# Revit family: QF_BOURGEAT_Lave_mains_cuve_ronde
name_source: partatom
category: Appareils sanitaires
revit_build: Autodesk Revit 2015 (Build: 20140606_1530(x64)
units: mm (PartAtom-declared; Revit-internal decimal feet)

## types (2) — shared parameters
Capacité de la cuve = 5 L
Certification = NF hygiene alimentaire
Diamètre de Raccordement Eau Adoucie = 21 mm
Diamètre de Raccordement Evacuation = 32 mm
Diamétre de la cuve = 275 mm
Débit Eau Adoucie = 0.2 L/s
Fabricant = BOURGEAT
Hauteur de la cuve = 125 mm  [stored 0.410105 ft]
Longueur hors tout = 340 mm  [stored 1.11549 ft]
Raccord = 15/21
Spécification du Fabricant = Lave mains à cuve ronde
URL catalogue = http://www.bourgeat.fr
zero-valued in all types: Hauteur de Raccordement Eau Adoucie du Sol Finis

## per-type parameters (varying)
| type | Dosseret | Hauteur hors tout | Modèle | Poids net à vide | Profondeur hors tout | position |
| Lave-mains sans dosseret | Non | 360 mm  [stored 1.1811 ft] | 849600 | 4.00 kg | 340 mm  [stored 1.11549 ft] | 1 mm  [stored 0.00328084 ft] |
| Lave-mains avec dosseret | Oui | 530 mm  [stored 1.73885 ft] | 849800 | 5.00 kg | 365 mm  [stored 1.19751 ft] | 23 mm  [stored 0.0754593 ft] |

note: [stored X ft] marks values corroborated as IEEE doubles in the binary element streams (Revit-internal decimal feet)
